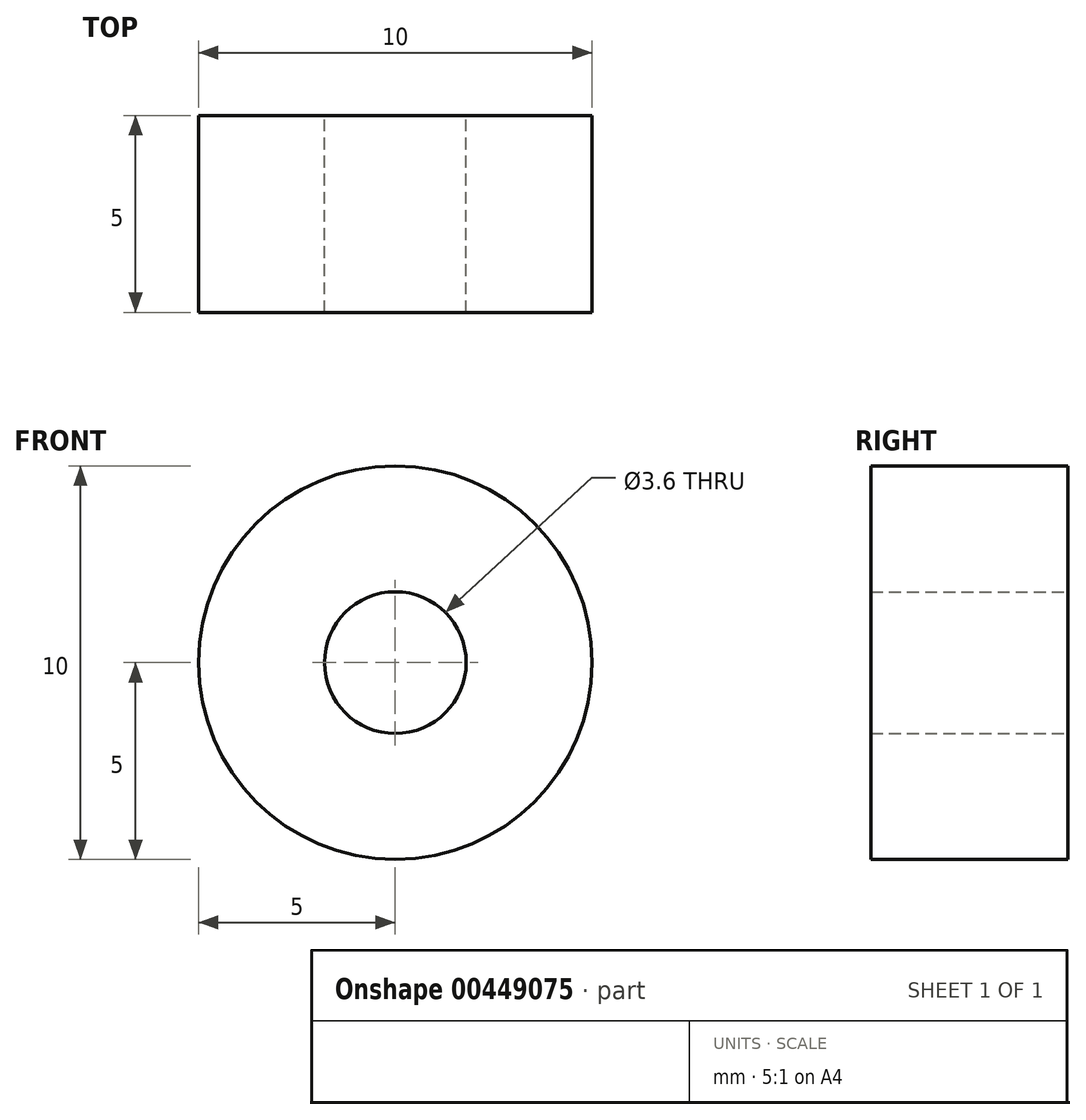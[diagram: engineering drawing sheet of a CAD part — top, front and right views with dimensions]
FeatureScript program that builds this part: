
annotation { "Feature Type Name" : "Feature", "Feature Type Description" : "" }
export const myFeature = defineFeature(function(context is Context, id is Id, definition is map)
    precondition{}
    {
        {
            var Q0;
            Q0=qCreatedBy(makeId("Front.planeOp"),FACE);
            var sketch = newSketch(context, id + "F0", { "sketchPlane" : qUnion([Q0])});
            skCircle(sketch, "E0", {"center": v(0, 0) * mm, "radius": 5 * mm});
            skCircle(sketch, "E1", {"center": v(0, 0) * mm, "radius": 1.8 * mm});
            skSolve(sketch);
        }
        {
            var Q0;
            Q0=makeQuery(id+"F0.imprint","IMPRINT",FACE,{"disambiguationData":[TD([[makeQuery(id+"F0.imprint","IMPRINT",EDGE,{"derivedFrom":sQuery(id+"F0.wireOp",EDGE,"E0")}),1.0]])]});
            extrude(context, id + "F1", {"entities" : qUnion([Q0]), "depth" : 5 * mm});
        }
    });
